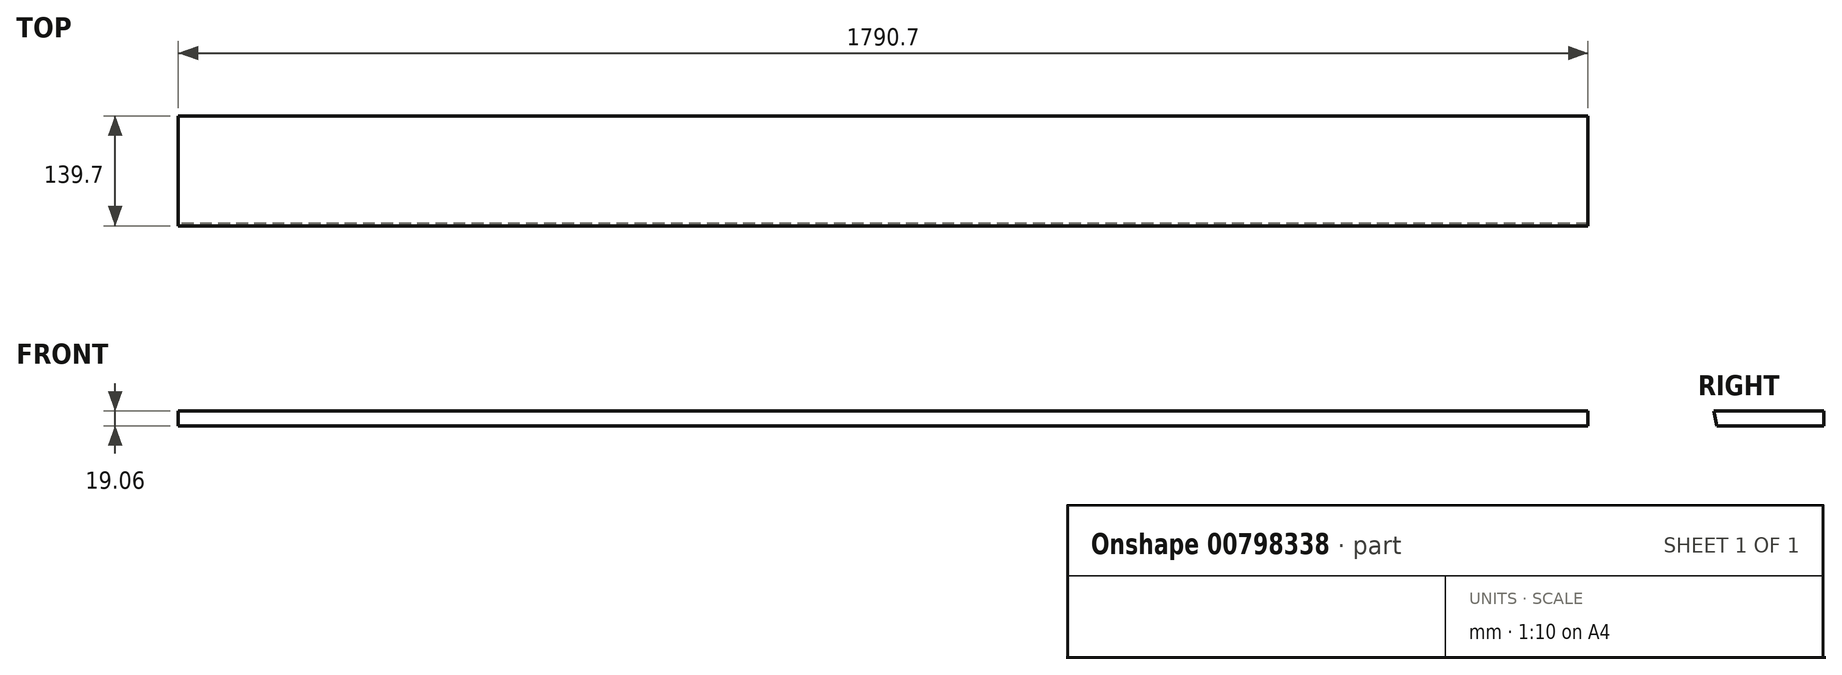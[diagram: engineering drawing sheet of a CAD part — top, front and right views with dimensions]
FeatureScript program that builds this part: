
annotation { "Feature Type Name" : "Feature", "Feature Type Description" : "" }
export const myFeature = defineFeature(function(context is Context, id is Id, definition is map)
    precondition{}
    {
        {
            var Q0;
            Q0=qCreatedBy(makeId("Right.planeOp"),FACE);
            var sketch = newSketch(context, id + "F0", { "sketchPlane" : qUnion([Q0])});
            skLineSegment(sketch, "E0.bottom", {"start": v(69.85, 9.53) * mm, "end": v(-69.85, 9.53) * mm});
            skLineSegment(sketch, "E0.top", {"start": v(69.85, -9.53) * mm, "end": v(-66.5, -9.53) * mm});
            skLineSegment(sketch, "E0.left", {"start": v(69.85, 9.53) * mm, "end": v(69.85, -9.53) * mm});
            skPoint(sketch, "E0.middle", {"position": v(0, 0) * mm});
            skLineSegment(sketch, "E1", {"start": v(-69.85, 9.53) * mm, "end": v(-66.5, -9.53) * mm});
            skPoint(sketch, "E0.right.end.orphan", {"position": v(-69.85, -9.53) * mm});
            skSolve(sketch);
        }
        {
            var Q0;
            Q0 = qSketchRegion(id + "F0", true);
            extrude(context, id + "F1", {"entities" : qUnion([Q0]), "depth" : 1790.7 * mm, "offsetDistance" : 25.4 * mm});
        }
    });
